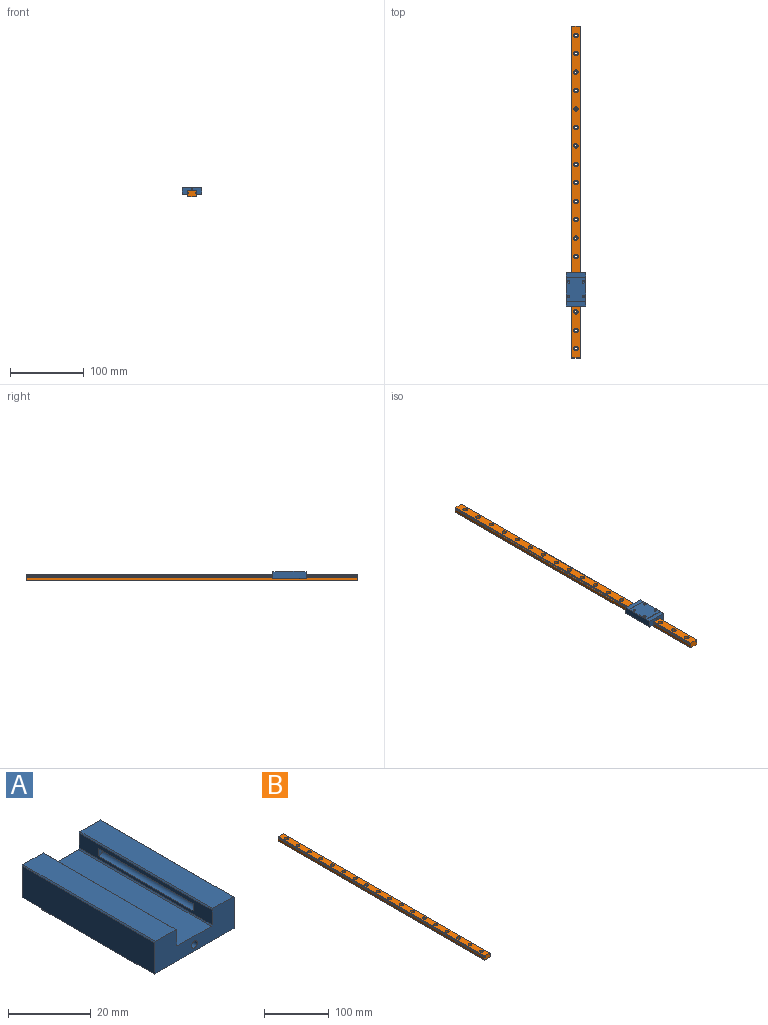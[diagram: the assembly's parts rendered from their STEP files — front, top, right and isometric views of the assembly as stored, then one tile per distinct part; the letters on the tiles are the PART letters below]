
ASSEMBLY  parts=2 mates=1
PART A: 37 faces, bbox 27x45.4x10 mm
  f0: plane 45.4x0.3mm, normal (-0.71,0,0.71), area 19.3mm2, adj f3,f6,f22,f23
  f1: plane 45.4x0.3mm, normal (0.71,0,0.71), area 19.3mm2, adj f10,f11,f22,f23
  f2: plane 45.4x0.3mm, normal (0.71,0,0.71), area 19.3mm2, adj f6,f7,f22,f23
  f3: plane 45.4x4.4mm, normal (-1,0,0), area 129.2mm2, adj f0,f5,f17,f20,f22,f23,f24
  f4: plane 45.4x11.4mm, normal (0,0,1), area 517.6mm2, adj f16,f17,f22,f23
  f5: cylinder r=1.15mm len=32.4mm, axis (0,-1,0), area 141.5mm2, adj f3,f20,f24
  f6: plane 45.4x6.9mm, normal (0,0,1), area 313.3mm2, adj f0,f2,f22,f23
  f7: plane 45.4x9.4mm, normal (1,0,0), area 424.2mm2, adj f2,f15,f18,f21,f22,f23,f25,f35
  f8: plane 32.4x26.4mm, normal (0,0,-1), area 821.1mm2, adj f14,f15,f18,f27,f29,f31,f33,f35
  f9: plane 45.4x9.4mm, normal (-1,0,0), area 424.2mm2, adj f14,f18,f21,f22,f23,f25,f34,f35
  f10: plane 45.4x6.9mm, normal (0,0,1), area 313.3mm2, adj f1,f22,f23,f34
  f11: plane 45.4x4.4mm, normal (1,0,0), area 129.2mm2, adj f1,f12,f16,f19,f22,f23,f36
  f12: cylinder r=1.15mm len=32.4mm, axis (0,-1,0), area 141.5mm2, adj f11,f19,f36
  f13: cylinder r=1mm len=45.4mm, axis (0,-1,0), area 285.3mm2, adj f22,f23
  f14: plane 32.4x0.3mm, normal (-0.71,0,-0.71), area 13.7mm2, adj f8,f9,f18,f35
  f15: plane 32.4x0.3mm, normal (0.71,0,-0.71), area 13.7mm2, adj f7,f8,f18,f35
  f16: plane 45.4x0.3mm, normal (0.71,0,0.71), area 19.3mm2, adj f4,f11,f22,f23
  f17: plane 45.4x0.3mm, normal (-0.71,0,0.71), area 19.3mm2, adj f3,f4,f22,f23
  f18: plane 27x0.5mm, normal (0,-1,0), area 13.4mm2, adj f7,f8,f9,f14,f15,f21
  f19: plane 2.3x1.52mm, normal (0,1,0), area 2.9mm2, adj f11,f12
  f20: plane 2.3x1.52mm, normal (0,1,0), area 2.9mm2, adj f3,f5
  f21: plane 27x6.5mm, normal (0,0,-1), area 175.5mm2, adj f7,f9,f18,f22
  f22: plane 27x9.5mm, normal (0,-1,0), area 193.3mm2, adj f0,f1,f2,f3,f4,f6,f7,f9
  f23: plane 27x9.5mm, normal (0,1,0), area 193.3mm2, adj f0,f1,f2,f3,f4,f6,f7,f9
  f24: plane 2.3x1.52mm, normal (0,-1,0), area 2.9mm2, adj f3,f5
  f25: plane 27x6.5mm, normal (0,0,-1), area 175.5mm2, adj f7,f9,f23,f35
  f26: cone r=857.17mm half-angle=59deg, axis (0,0,-1), area 10mm2, adj f27
  f27: cylinder r=1.65mm len=3.5mm, axis (0,0,1), area 36.3mm2, adj f8,f26
  f28: cone r=857.17mm half-angle=59deg, axis (0,0,-1), area 10mm2, adj f29
  f29: cylinder r=1.65mm len=3.5mm, axis (0,0,1), area 36.3mm2, adj f8,f28
  f30: cone r=857.17mm half-angle=59deg, axis (0,0,-1), area 10mm2, adj f31
  f31: cylinder r=1.65mm len=3.5mm, axis (0,0,1), area 36.3mm2, adj f8,f30
  f32: cone r=857.17mm half-angle=59deg, axis (0,0,-1), area 10mm2, adj f33
  f33: cylinder r=1.65mm len=3.5mm, axis (0,0,1), area 36.3mm2, adj f8,f32
  f34: plane 45.4x0.3mm, normal (-0.71,0,0.71), area 19.3mm2, adj f9,f10,f22,f23
  f35: plane 27x0.5mm, normal (0,1,0), area 13.4mm2, adj f7,f8,f9,f14,f15,f25
  f36: plane 2.3x1.52mm, normal (0,-1,0), area 2.9mm2, adj f11,f12
PART B: 76 faces, bbox 12x450x8 mm
  f0: plane 450x0.51mm, normal (0,0,1), area 229.4mm2, adj f1,f19,f20,f51
  f1: plane 450x0.3mm, normal (1,0,0), area 135mm2, adj f0,f2,f20,f51
  f2: plane 450x0.51mm, normal (0,0,-1), area 229.4mm2, adj f1,f3,f20,f51
  f3: cylinder r=1.15mm len=450mm, axis (0,1,0), area 575.7mm2, adj f2,f4,f20,f51
  f4: plane 450x0.86mm, normal (1,0,0), area 387.4mm2, adj f3,f5,f20,f51
  f5: plane 450x0.35mm, normal (0.71,0,0.71), area 222.7mm2, adj f4,f6,f20,f51
  f6: plane 450x11.3mm, normal (0,0,1), area 4576.1mm2, adj f5,f7,f20,f23,f26,f29,f32,f35
  f7: plane 450x0.35mm, normal (-0.71,0,0.71), area 222.7mm2, adj f6,f8,f20,f51
  f8: plane 450x0.86mm, normal (-1,0,0), area 387.4mm2, adj f7,f9,f20,f51
  f9: cylinder r=1.15mm len=450mm, axis (0,1,0), area 575.7mm2, adj f8,f10,f20,f51
  f10: plane 450x0.51mm, normal (0,0,-1), area 229.4mm2, adj f9,f11,f20,f51
  f11: plane 450x0.3mm, normal (-1,0,0), area 135mm2, adj f10,f12,f20,f51
  f12: plane 450x0.51mm, normal (0,0,1), area 229.4mm2, adj f11,f13,f20,f51
  f13: cylinder r=1.15mm len=450mm, axis (0,1,0), area 575.7mm2, adj f12,f14,f20,f51
  f14: plane 450x4.26mm, normal (-1,0,0), area 1917.6mm2, adj f13,f15,f20,f51
  f15: plane 450x0.35mm, normal (-0.71,0,-0.71), area 222.7mm2, adj f14,f16,f20,f51
  f16: plane 450x11.3mm, normal (0,0,-1), area 4911.8mm2, adj f15,f17,f20,f21,f24,f27,f30,f33
  f17: plane 450x0.35mm, normal (0.71,0,-0.71), area 222.7mm2, adj f16,f18,f20,f51
  f18: plane 450x4.26mm, normal (1,0,0), area 1917.6mm2, adj f17,f19,f20,f51
  f19: cylinder r=1.15mm len=450mm, axis (0,1,0), area 575.7mm2, adj f0,f18,f20,f51
  f20: plane 12x8mm, normal (0,-1,0), area 93mm2, adj f0,f1,f2,f3,f4,f5,f6,f7
  f21: cylinder r=1.75mm len=3.5mm, axis (0,0,1), area 38.5mm2, adj f16,f22
  f22: plane 6x6mm, normal (0,0,1), area 18.7mm2, adj f21,f23
  f23: cylinder r=3mm len=6mm, axis (0,0,1), area 84.8mm2, adj f6,f22
  f24: cylinder r=1.75mm len=3.5mm, axis (0,0,1), area 38.5mm2, adj f16,f25
  f25: plane 6x6mm, normal (0,0,1), area 18.7mm2, adj f24,f26
  f26: cylinder r=3mm len=6mm, axis (0,0,1), area 84.8mm2, adj f6,f25
  f27: cylinder r=1.75mm len=3.5mm, axis (0,0,1), area 38.5mm2, adj f16,f28
  f28: plane 6x6mm, normal (0,0,1), area 18.7mm2, adj f27,f29
  f29: cylinder r=3mm len=6mm, axis (0,0,1), area 84.8mm2, adj f6,f28
  f30: cylinder r=1.75mm len=3.5mm, axis (0,0,1), area 38.5mm2, adj f16,f31
  f31: plane 6x6mm, normal (0,0,1), area 18.7mm2, adj f30,f32
  f32: cylinder r=3mm len=6mm, axis (0,0,1), area 84.8mm2, adj f6,f31
  f33: cylinder r=1.75mm len=3.5mm, axis (0,0,1), area 38.5mm2, adj f16,f34
  f34: plane 6x6mm, normal (0,0,1), area 18.7mm2, adj f33,f35
  f35: cylinder r=3mm len=6mm, axis (0,0,1), area 84.8mm2, adj f6,f34
  f36: cylinder r=1.75mm len=3.5mm, axis (0,0,1), area 38.5mm2, adj f16,f37
  f37: plane 6x6mm, normal (0,0,1), area 18.7mm2, adj f36,f38
  f38: cylinder r=3mm len=6mm, axis (0,0,1), area 84.8mm2, adj f6,f37
  f39: cylinder r=1.75mm len=3.5mm, axis (0,0,1), area 38.5mm2, adj f16,f40
  f40: plane 6x6mm, normal (0,0,1), area 18.7mm2, adj f39,f41
  f41: cylinder r=3mm len=6mm, axis (0,0,1), area 84.8mm2, adj f6,f40
  f42: cylinder r=1.75mm len=3.5mm, axis (0,0,1), area 38.5mm2, adj f16,f43
  f43: plane 6x6mm, normal (0,0,1), area 18.7mm2, adj f42,f44
  f44: cylinder r=3mm len=6mm, axis (0,0,1), area 84.8mm2, adj f6,f43
  f45: cylinder r=1.75mm len=3.5mm, axis (0,0,1), area 38.5mm2, adj f16,f46
  f46: plane 6x6mm, normal (0,0,1), area 18.7mm2, adj f45,f47
  f47: cylinder r=3mm len=6mm, axis (0,0,1), area 84.8mm2, adj f6,f46
  f48: cylinder r=1.75mm len=3.5mm, axis (0,0,1), area 38.5mm2, adj f16,f49
  f49: plane 6x6mm, normal (0,0,1), area 18.7mm2, adj f48,f50
  f50: cylinder r=3mm len=6mm, axis (0,0,1), area 84.8mm2, adj f6,f49
  f51: plane 12x8mm, normal (0,1,0), area 93mm2, adj f0,f1,f2,f3,f4,f5,f6,f7
  f52: cylinder r=1.75mm len=3.5mm, axis (0,0,1), area 38.5mm2, adj f16,f53
  f53: plane 6x6mm, normal (0,0,1), area 18.7mm2, adj f52,f54
  f54: cylinder r=3mm len=6mm, axis (0,0,1), area 84.8mm2, adj f6,f53
  f55: cylinder r=1.75mm len=3.5mm, axis (0,0,1), area 38.5mm2, adj f16,f56
  f56: plane 6x6mm, normal (0,0,1), area 18.7mm2, adj f55,f57
  f57: cylinder r=3mm len=6mm, axis (0,0,1), area 84.8mm2, adj f6,f56
  f58: cylinder r=1.75mm len=3.5mm, axis (0,0,1), area 38.5mm2, adj f16,f59
  f59: plane 6x6mm, normal (0,0,1), area 18.7mm2, adj f58,f60
  f60: cylinder r=3mm len=6mm, axis (0,0,1), area 84.8mm2, adj f6,f59
  f61: cylinder r=1.75mm len=3.5mm, axis (0,0,1), area 38.5mm2, adj f16,f62
  f62: plane 6x6mm, normal (0,0,1), area 18.7mm2, adj f61,f63
  f63: cylinder r=3mm len=6mm, axis (0,0,1), area 84.8mm2, adj f6,f62
  f64: cylinder r=1.75mm len=3.5mm, axis (0,0,1), area 38.5mm2, adj f16,f65
  f65: plane 6x6mm, normal (0,0,1), area 18.7mm2, adj f64,f66
  f66: cylinder r=3mm len=6mm, axis (0,0,1), area 84.8mm2, adj f6,f65
  f67: cylinder r=1.75mm len=3.5mm, axis (0,0,1), area 38.5mm2, adj f16,f68
  f68: plane 6x6mm, normal (0,0,1), area 18.7mm2, adj f67,f69
  f69: cylinder r=3mm len=6mm, axis (0,0,1), area 84.8mm2, adj f6,f68
  f70: cylinder r=1.75mm len=3.5mm, axis (0,0,1), area 38.5mm2, adj f16,f71
  f71: plane 6x6mm, normal (0,0,1), area 18.7mm2, adj f70,f72
  f72: cylinder r=3mm len=6mm, axis (0,0,1), area 84.8mm2, adj f6,f71
  f73: cylinder r=1.75mm len=3.5mm, axis (0,0,1), area 38.5mm2, adj f16,f74
  f74: plane 6x6mm, normal (0,0,1), area 18.7mm2, adj f73,f75
  f75: cylinder r=3mm len=6mm, axis (0,0,1), area 84.8mm2, adj f6,f74
PLACE A rot(axis=(0,1,0),180deg) t=(-17.05,127.24,13.68)mm
PLACE B t=(-17.05,43,13.68)mm
MATE slider B.f20 <-> A.f22  axis (0,-1,0) through (-17.05,18,13.68)mm
